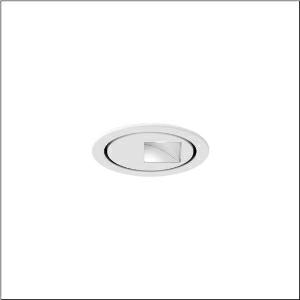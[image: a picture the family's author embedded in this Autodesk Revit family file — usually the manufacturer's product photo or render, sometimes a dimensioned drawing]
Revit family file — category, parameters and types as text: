
# Revit family: lunis_11_micro_round_51dj11b71wm21
name_source: partatom
category: Lighting Fixtures
units: mm (PartAtom-declared; Revit-internal decimal feet)

## family parameters
Cut with Voids When Loaded = No
Host = Face
Light Source = No
Part Type = Normal
Room Calculation Point = No
Round Connector Dimension = Use Diameter
Shared = No

## types (1)
- Lunis 11 micro round (1 x LED 3000K / CRI = 90 (unbekannt), 1100 lm, 3000K)
    Apparent Load = 20 VA
    CIE Flux Codes = 42 75 96 100 100
    Color Rendering = 90
    Color Temperature = 3000K
    Default Elevation = 1800 mm
    Description = Lunis 11 micro round, downlight, light control with wallwasher, of highly reflective aluminium, highly specular, light emission: direct distribution, LED rated luminous flux: 1.100lm, light colour: 930, with terminal, 3-pole, mains connection: 220..230V, AC, 50/60Hz, LED module, of aluminium, highly specular, white, diameter: 114mm, clamping range: 1..40mm, recessing ring, of plastic, traffic white (RAL 9016), protection rating (complete): IP20, insulation class (complete): insulation class II (safety insulation), certification: CE, permissible ambient temperature for indoor applications: 0..+35°C, packaging unit: 1 piece
    Height = 0 mm  [stored 0 ft]
    Lamp = 1 x LED 3000K / CRI >= 90 (unbekannt)
    Lamp Light Flux = 1100 lm
    Lamp count = 1
    Length = 114 mm
    Luminous efficacy = 56 lm/W
    Manufacturer = Siteco
    ModVariant = No
    Model = 51DJ11B71WM21
    Mounting Place = Ceiling
    Mounting Type = Recessed
    Number of Poles = 1
    OnlyDefault = Yes
    Power Factor = 1
    Product Name = Lunis 11 micro round
    Product group = downlight
    ProductGroupID = 400
    Protection Class = Protection class II
    Protection Degree = IP 20
    RLX_Detail_Level = 1
    RLX_Emergency_Light_Flux = 0 lm
    RLX_Emergency_Type = 0
    RLX_Emergency_Type_DB = No
    RlxData = <blob elided: 40493 chars, md5=4a0401da>
    Socket = socket
    Standby Power = 0 W
    System Light Flux = 1100 lm
    System Power = 20 W
    Type Comments = Product without accessories
    Type Image = l_1004773.jpg
    URL = http://relux.com
    VarID = ---
    Voltage = 0 V
    Weight = 0.00 kg
    Width = 114 mm

note: [stored X ft] marks values corroborated as IEEE doubles in the binary element streams (Revit-internal decimal feet)

## geometry (parser evidence)
native form markers: Blend x4, Sweep x10
no freeform markers — native parametric forms only
